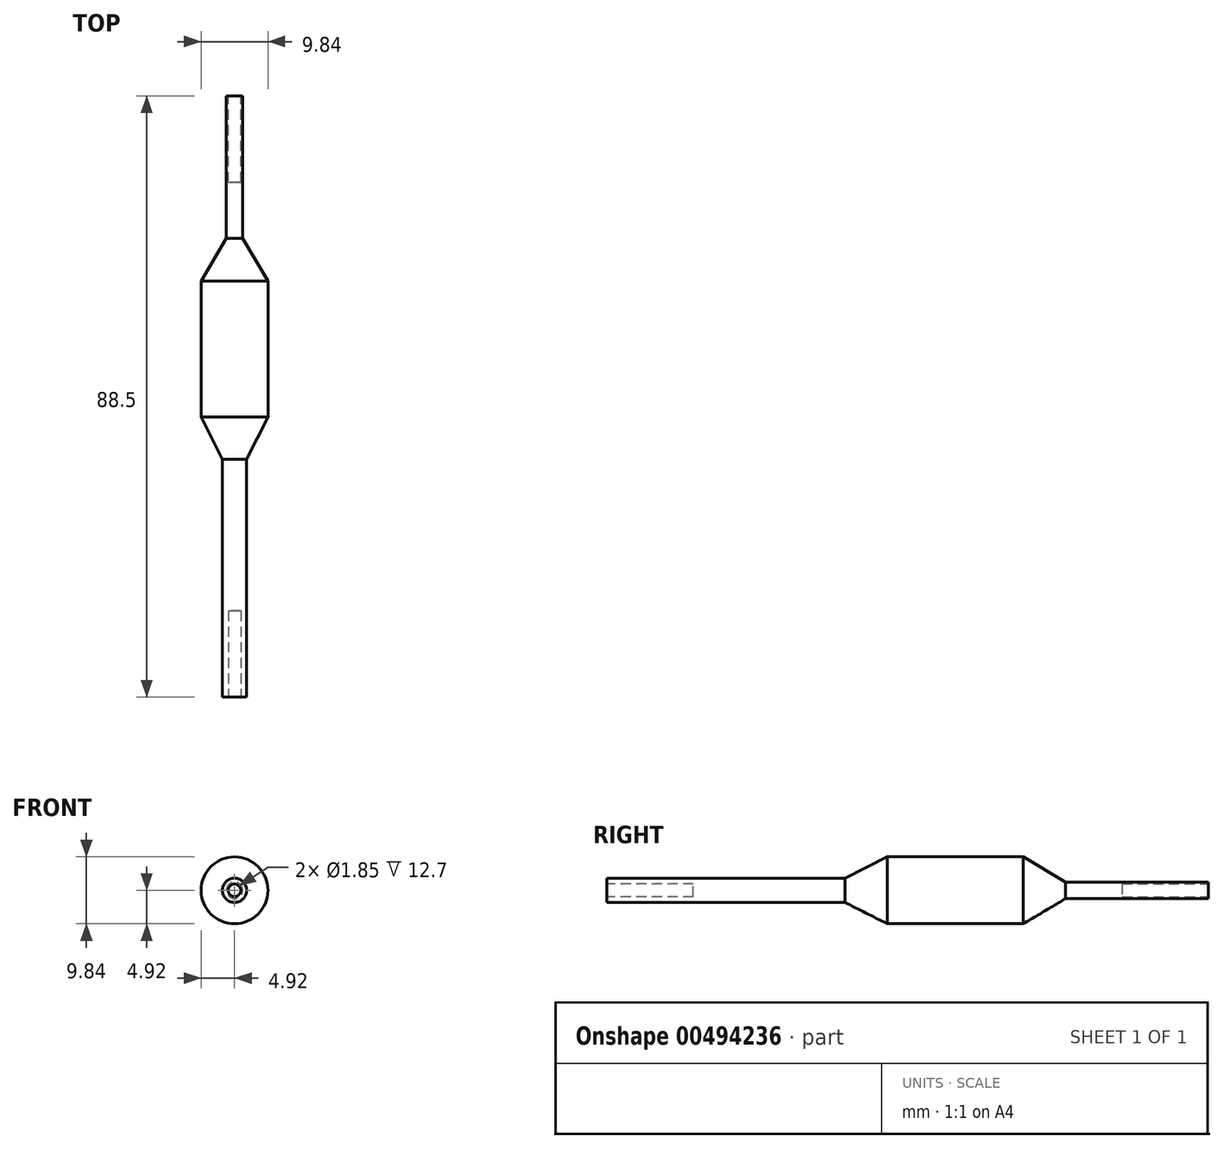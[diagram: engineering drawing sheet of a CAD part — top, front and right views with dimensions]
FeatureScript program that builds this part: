
annotation { "Feature Type Name" : "Feature", "Feature Type Description" : "" }
export const myFeature = defineFeature(function(context is Context, id is Id, definition is map)
    precondition{}
    {
        {
            var Q0;
            Q0=qCreatedBy(makeId("Right.planeOp"),FACE);
            var sketch = newSketch(context, id + "F0", { "sketchPlane" : qUnion([Q0])});
            skLineSegment(sketch, "E0", {"start": v(0, 0) * mm, "end": v(0, 1.78) * mm});
            skLineSegment(sketch, "E1", {"start": v(0, 1.78) * mm, "end": v(35, 1.78) * mm});
            skLineSegment(sketch, "E2", {"start": v(35, 1.78) * mm, "end": v(41.25, 4.92) * mm});
            skLineSegment(sketch, "E3", {"start": v(41.25, 4.92) * mm, "end": v(61.25, 4.92) * mm});
            skLineSegment(sketch, "E4", {"start": v(61.25, 4.92) * mm, "end": v(67.5, 1.2) * mm});
            skLineSegment(sketch, "E5", {"start": v(67.5, 1.2) * mm, "end": v(88.5, 1.2) * mm});
            skLineSegment(sketch, "E6", {"start": v(88.5, 1.2) * mm, "end": v(88.5, 0) * mm});
            skLineSegment(sketch, "E7", {"start": v(0, 0) * mm, "end": v(88.5, 0) * mm, "construction": true});
            skLineSegment(sketch, "E8", {"start": v(0, 0) * mm, "end": v(88.5, 0) * mm});
            skSolve(sketch);
        }
        {
            var Q0;
            Q0=qSketchRegion(id+"F0",true);
            var Q1;
            Q1=sQuery(id+"F0.wireOp",EDGE,"E7");
            revolve(context, id + "F1", {"entities" : qUnion([Q0]), "axis" : qUnion([Q1]), "revolveType" : RevolveType.FULL});
        }
        {
            var Q0;
            Q0=makeQuery(id+"F1.opRevolve","SWEPT_FACE",FACE,{"disambiguationData":[OSD([sQuery(id+"F0.wireOp",EDGE,"E0")])]});
            var sketch = newSketch(context, id + "F2", { "sketchPlane" : qUnion([Q0])});
            skCircle(sketch, "E9", {"center": v(0, 0) * mm, "radius": 0.93 * mm});
            skSolve(sketch);
        }
        {
            var Q0;
            Q0=qSketchRegion(id+"F2",true);
            extrude(context, id + "F3", {"entities" : qUnion([Q0]), "operationType" : NewBodyOperationType.REMOVE, "oppositeDirection" : true, "depth" : 12.7 * mm});
        }
        {
            var Q0;
            Q0=makeQuery(id+"F1.opRevolve","SWEPT_FACE",FACE,{"disambiguationData":[OSD([sQuery(id+"F0.wireOp",EDGE,"E6")])]});
            var sketch = newSketch(context, id + "F4", { "sketchPlane" : qUnion([Q0])});
            skCircle(sketch, "E10", {"center": v(0, 0) * mm, "radius": 0.93 * mm});
            skSolve(sketch);
        }
        {
            var Q0;
            Q0=qSketchRegion(id+"F4",true);
            extrude(context, id + "F5", {"entities" : qUnion([Q0]), "operationType" : NewBodyOperationType.REMOVE, "oppositeDirection" : true, "depth" : 12.7 * mm});
        }
    });
